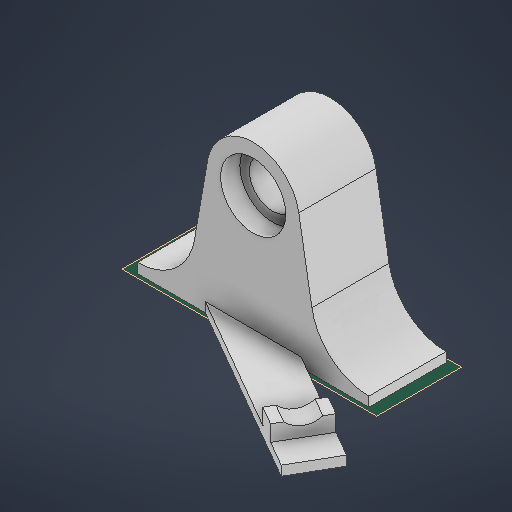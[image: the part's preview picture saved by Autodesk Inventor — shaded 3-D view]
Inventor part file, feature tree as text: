
AUTODESK INVENTOR PART (.ipt)
format: ipt  version: 2025.3 (Build 293356030, 356C)  size: 271,872 bytes
history: native  units: mm
features: extrude x7, sketch x3, plane x1, projected_geometry x1
ambient origin geometry x8: Origin, YZ Plane, XZ Plane, XY Plane, X Axis, Y Axis, Z Axis, Center Point
bodies: Solid1 (feature_tree)
feature tree (12):
  sketch  "Sketch1"  dims[d0=16.9mm d1=12.0mm d2=30.0mm d3=12.0mm d4=15.0mm d5=60.0mm d6=2.5mm d7=20.0mm d8=0.0mm]
  extrude  "Extrusion1"  Depth=20.0mm TaperAngle=0.0deg
  extrude  "Extrusion2"  Depth=20.0mm TaperAngle=0.0deg
  extrude  "Extrusion3"  TaperAngle=60.0deg  [1 undecoded]
  plane  "Work Plane1"
  sketch  "Sketch2"  dims[d9=15.0mm d10=0.0mm d11=20.0mm d12=0.0mm]
  extrude  "Extrusion6"  Depth=5.5mm
  sketch  "Sketch4"  dims[d13=0.0mm d14=60.0deg d16=5.5mm d17=20.0mm d26=30.0mm d27=2.5mm d28=0.0mm d29=14.6mm d30=10.7mm d31=1.5mm d32=8.0mm d33=5.5mm d34=0.0mm d35=5.5mm d36=0.0mm d37=7.5mm d38=0.0mm]
  extrude  "Extrusion7"  Depth=20.0mm
  extrude  "Extrusion8"  Depth=30.0mm
  extrude  "Extrusion9"  Depth=2.5mm TaperAngle=0.0deg
  projected_geometry  "Projected Loop2"
note: 1 required parameter value undecoded (feature->parameter linkage not recoverable at this tier; creation-order binding heuristic only, values carry confidence <= 0.55)
